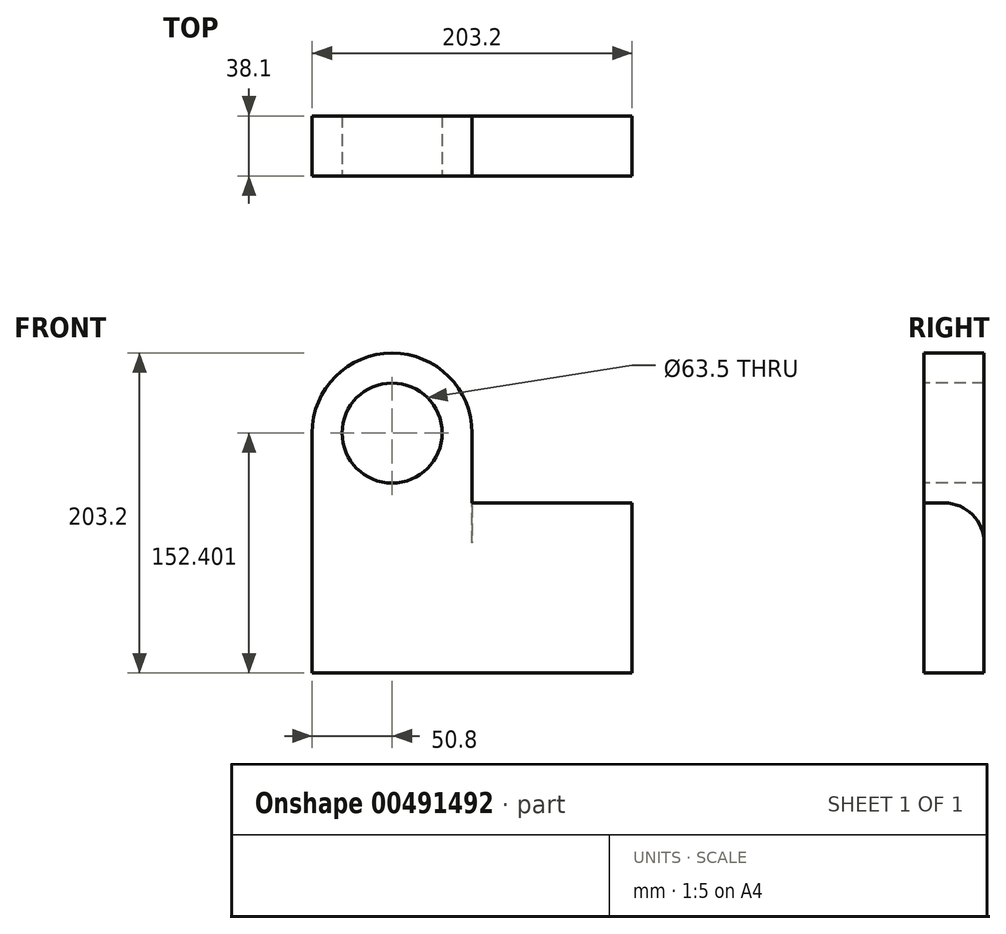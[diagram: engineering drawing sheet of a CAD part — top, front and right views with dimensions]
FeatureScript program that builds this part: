
annotation { "Feature Type Name" : "Feature", "Feature Type Description" : "" }
export const myFeature = defineFeature(function(context is Context, id is Id, definition is map)
    precondition{}
    {
        {
            var Q0;
            Q0=qCreatedBy(makeId("Front.planeOp"),FACE);
            var sketch = newSketch(context, id + "F0", { "sketchPlane" : qUnion([Q0])});
            skLineSegment(sketch, "E0", {"start": v(-129.2, 62.4) * mm, "end": v(-129.2, -90) * mm});
            skLineSegment(sketch, "E1", {"start": v(-129.2, -90) * mm, "end": v(74, -90) * mm});
            skLineSegment(sketch, "E2", {"start": v(74, -90) * mm, "end": v(74, 17.94) * mm});
            skArc(sketch, "E3", {"start": v(-27.6, 62.4) * mm, "mid": v(-78.4, 113.2) * mm, "end": v(-129.2, 62.4) * mm});
            skLineSegment(sketch, "E4", {"start": v(-27.6, 62.4) * mm, "end": v(-27.6, 17.94) * mm});
            skLineSegment(sketch, "E5", {"start": v(-27.6, 17.94) * mm, "end": v(74, 17.94) * mm});
            skSolve(sketch);
        }
        {
            var Q0;
            Q0=makeQuery(id+"F0.imprint","IMPRINT",FACE,{"disambiguationData":[TD([[makeQuery(id+"F0.imprint","IMPRINT",EDGE,{"derivedFrom":sQuery(id+"F0.wireOp",EDGE,"E0")}),1.0]])]});
            extrude(context, id + "F1", {"entities" : qUnion([Q0]), "depth" : 38.1 * mm});
        }
        {
            var Q0;
            Q0=makeQuery(id+"F1.opExtrude","CAP_EDGE",EDGE,{"disambiguationData":[OSD([sQuery(id+"F0.wireOp",EDGE,"E5")])],"isStart":true});
            fillet(context, id + "F2", {"entities" : qUnion([Q0]), "radius" : 25.4 * mm, "tangentPropagation" : true, "allowEdgeOverflow" : false});
        }
        {
            var Q0;
            Q0=makeQuery(id+"F1.opExtrude","CAP_FACE",FACE,{"disambiguationData":[OSD([sQuery(id+"F0.wireOp",EDGE,"E0"),sQuery(id+"F0.wireOp",EDGE,"E1"),sQuery(id+"F0.wireOp",EDGE,"E2"),sQuery(id+"F0.wireOp",EDGE,"E3"),sQuery(id+"F0.wireOp",EDGE,"E4"),sQuery(id+"F0.wireOp",EDGE,"E5")])],"isStart":false});
            var sketch = newSketch(context, id + "F3", { "sketchPlane" : qUnion([Q0])});
            skCircle(sketch, "E6", {"center": v(-78.4, 62.4) * mm, "radius": 31.75 * mm});
            skSolve(sketch);
        }
        {
            var Q0;
            Q0=qSketchRegion(id+"F3",true);
            extrude(context, id + "F4", {"entities" : qUnion([Q0]), "operationType" : NewBodyOperationType.REMOVE, "oppositeDirection" : true, "depth" : 50.8 * mm});
        }
    });
